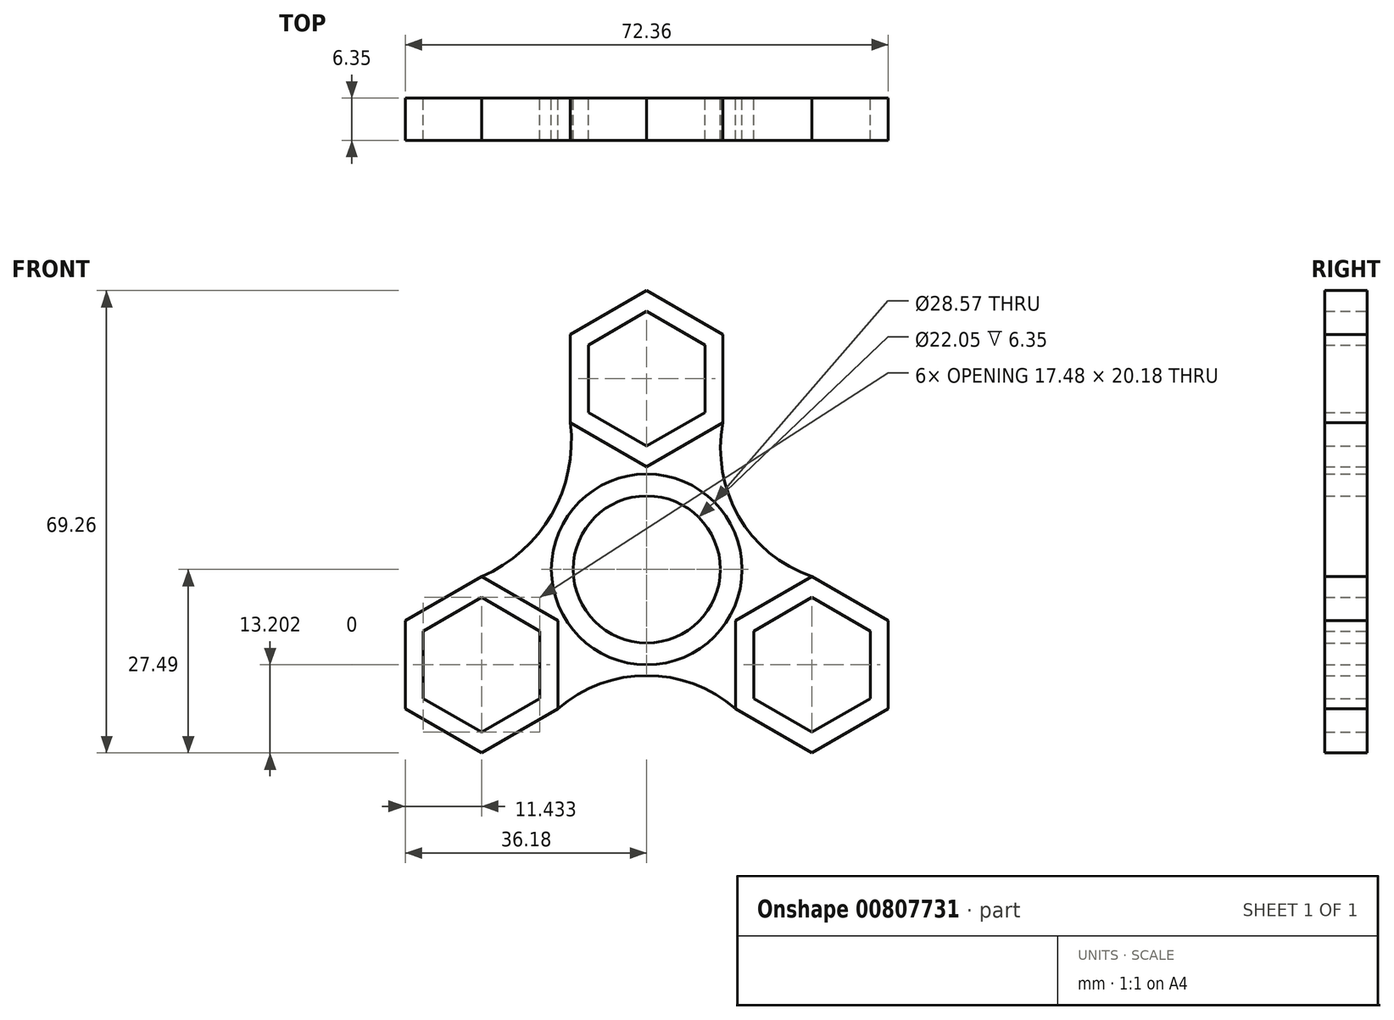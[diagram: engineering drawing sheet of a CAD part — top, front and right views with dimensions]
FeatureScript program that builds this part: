
annotation { "Feature Type Name" : "Feature", "Feature Type Description" : "" }
export const myFeature = defineFeature(function(context is Context, id is Id, definition is map)
    precondition{}
    {
        {
            var Q0;
            Q0=qCreatedBy(makeId("Front.planeOp"),FACE);
            var sketch = newSketch(context, id + "F0", { "sketchPlane" : qUnion([Q0])});
            skCircle(sketch, "E0", {"center": v(0, 0) * mm, "radius": 14.29 * mm});
            skCircle(sketch, "E1", {"center": v(0, 0) * mm, "radius": 11.02 * mm});
            skCircle(sketch, "E2.cCircle", {"center": v(0, 28.58) * mm, "radius": 8.74 * mm, "construction": true});
            skLineSegment(sketch, "E2.0", {"start": v(-8.74, 23.53) * mm, "end": v(-8.74, 33.62) * mm});
            skLineSegment(sketch, "E2.1", {"start": v(-8.74, 33.62) * mm, "end": v(0, 38.66) * mm});
            skLineSegment(sketch, "E2.2", {"start": v(0, 38.66) * mm, "end": v(8.74, 33.62) * mm});
            skLineSegment(sketch, "E2.3", {"start": v(8.74, 33.62) * mm, "end": v(8.74, 23.53) * mm});
            skLineSegment(sketch, "E2.4", {"start": v(8.74, 23.53) * mm, "end": v(0, 18.49) * mm});
            skLineSegment(sketch, "E2.5", {"start": v(0, 18.49) * mm, "end": v(-8.74, 23.53) * mm});
            skPoint(sketch, "E2.0.midPoint", {"position": v(-8.74, 28.58) * mm});
            skCircle(sketch, "E3.cCircle", {"center": v(0, 28.58) * mm, "radius": 11.43 * mm, "construction": true});
            skLineSegment(sketch, "E3.0", {"start": v(-11.43, 21.98) * mm, "end": v(-11.43, 35.17) * mm});
            skLineSegment(sketch, "E3.1", {"start": v(-11.43, 35.17) * mm, "end": v(0, 41.77) * mm});
            skLineSegment(sketch, "E3.2", {"start": v(0, 41.77) * mm, "end": v(11.43, 35.17) * mm});
            skLineSegment(sketch, "E3.3", {"start": v(11.43, 35.17) * mm, "end": v(11.43, 21.98) * mm});
            skLineSegment(sketch, "E3.4", {"start": v(11.43, 21.98) * mm, "end": v(0, 15.38) * mm});
            skLineSegment(sketch, "E3.5", {"start": v(0, 15.38) * mm, "end": v(-11.43, 21.98) * mm});
            skPoint(sketch, "E3.0.midPoint", {"position": v(-11.43, 28.58) * mm});
            skLineSegment(sketch, "E4.1.0", {"start": v(-24.75, -24.38) * mm, "end": v(-33.48, -19.33) * mm});
            skLineSegment(sketch, "E4.1.1", {"start": v(-36.18, -7.69) * mm, "end": v(-24.75, -1.09) * mm});
            skLineSegment(sketch, "E4.1.2", {"start": v(-24.75, -1.09) * mm, "end": v(-13.32, -7.69) * mm});
            skLineSegment(sketch, "E4.1.3", {"start": v(-13.32, -7.69) * mm, "end": v(-13.32, -20.89) * mm});
            skLineSegment(sketch, "E4.1.4", {"start": v(-33.48, -19.33) * mm, "end": v(-33.48, -9.24) * mm});
            skPoint(sketch, "E4.1.7", {"position": v(-19.03, -24.19) * mm});
            skCircle(sketch, "E4.1.8", {"center": v(-24.75, -14.29) * mm, "radius": 8.74 * mm, "construction": true});
            skLineSegment(sketch, "E4.1.9", {"start": v(-33.48, -9.24) * mm, "end": v(-24.75, -4.2) * mm});
            skLineSegment(sketch, "E4.1.10", {"start": v(-24.75, -4.2) * mm, "end": v(-16, -9.24) * mm});
            skLineSegment(sketch, "E4.1.11", {"start": v(-16, -9.24) * mm, "end": v(-16, -19.33) * mm});
            skCircle(sketch, "E4.1.12", {"center": v(-24.75, -14.29) * mm, "radius": 11.43 * mm, "construction": true});
            skLineSegment(sketch, "E4.1.13", {"start": v(-13.32, -20.89) * mm, "end": v(-24.75, -27.49) * mm});
            skLineSegment(sketch, "E4.1.14", {"start": v(-24.75, -27.49) * mm, "end": v(-36.18, -20.89) * mm});
            skLineSegment(sketch, "E4.1.15", {"start": v(-36.18, -20.89) * mm, "end": v(-36.18, -7.69) * mm});
            skPoint(sketch, "E4.1.16", {"position": v(-20.38, -21.85) * mm});
            skLineSegment(sketch, "E4.1.17", {"start": v(-16, -19.33) * mm, "end": v(-24.75, -24.38) * mm});
            skLineSegment(sketch, "E4.2.0", {"start": v(33.48, -9.24) * mm, "end": v(33.48, -19.33) * mm});
            skLineSegment(sketch, "E4.2.1", {"start": v(24.75, -27.49) * mm, "end": v(13.32, -20.89) * mm});
            skLineSegment(sketch, "E4.2.2", {"start": v(13.32, -20.89) * mm, "end": v(13.32, -7.69) * mm});
            skLineSegment(sketch, "E4.2.3", {"start": v(13.32, -7.69) * mm, "end": v(24.75, -1.09) * mm});
            skLineSegment(sketch, "E4.2.4", {"start": v(33.48, -19.33) * mm, "end": v(24.75, -24.38) * mm});
            skPoint(sketch, "E4.2.7", {"position": v(30.46, -4.39) * mm});
            skCircle(sketch, "E4.2.8", {"center": v(24.75, -14.29) * mm, "radius": 8.74 * mm, "construction": true});
            skLineSegment(sketch, "E4.2.9", {"start": v(24.75, -24.38) * mm, "end": v(16, -19.33) * mm});
            skLineSegment(sketch, "E4.2.10", {"start": v(16, -19.33) * mm, "end": v(16, -9.24) * mm});
            skLineSegment(sketch, "E4.2.11", {"start": v(16, -9.24) * mm, "end": v(24.75, -4.2) * mm});
            skCircle(sketch, "E4.2.12", {"center": v(24.75, -14.29) * mm, "radius": 11.43 * mm, "construction": true});
            skLineSegment(sketch, "E4.2.13", {"start": v(24.75, -1.09) * mm, "end": v(36.18, -7.69) * mm});
            skLineSegment(sketch, "E4.2.14", {"start": v(36.18, -7.69) * mm, "end": v(36.18, -20.89) * mm});
            skLineSegment(sketch, "E4.2.15", {"start": v(36.18, -20.89) * mm, "end": v(24.75, -27.49) * mm});
            skPoint(sketch, "E4.2.16", {"position": v(29.12, -6.72) * mm});
            skLineSegment(sketch, "E4.2.17", {"start": v(24.75, -4.2) * mm, "end": v(33.48, -9.24) * mm});
            skArc(sketch, "E5", {"start": v(11.43, 21.98) * mm, "mid": v(13.77, 7.95) * mm, "end": v(24.75, -1.09) * mm});
            skArc(sketch, "E6", {"start": v(-24.75, -1.09) * mm, "mid": v(-14.26, 8.23) * mm, "end": v(-11.43, 21.98) * mm});
            skArc(sketch, "E7", {"start": v(13.32, -20.89) * mm, "mid": v(0, -15.9) * mm, "end": v(-13.32, -20.89) * mm});
            skSolve(sketch);
        }
        {
            var Q0;
            Q0=makeQuery(id+"F0.imprint","IMPRINT",FACE,{"disambiguationData":[TD([[makeQuery(id+"F0.imprint","IMPRINT",EDGE,{"derivedFrom":sQuery(id+"F0.wireOp",EDGE,"E2.0")}),-1.0]])]});
            var sketch = newSketch(context, id + "F1", { "sketchPlane" : qUnion([Q0])});
            skArc(sketch, "E8", {"start": v(11.48, 22.04) * mm, "mid": v(12.38, 7.19) * mm, "end": v(24.77, -1.05) * mm});
            skArc(sketch, "E9", {"start": v(-24.76, -1.04) * mm, "mid": v(-12.38, 7.18) * mm, "end": v(-11.44, 22) * mm});
            skArc(sketch, "E10", {"start": v(13.38, -20.88) * mm, "mid": v(0.07, -14.3) * mm, "end": v(-13.26, -20.84) * mm});
            skSolve(sketch);
        }
        {
            var Q0;
            Q0 = qSketchRegion(id + "F1", true);
            var Q1;
            Q1=makeQuery(id+"F0.imprint","IMPRINT",FACE,{"disambiguationData":[TD([[makeQuery(id+"F0.imprint","IMPRINT",EDGE,{"derivedFrom":sQuery(id+"F0.wireOp",EDGE,"E4.1.0")}),1.0]])]});
            var Q2;
            Q2=makeQuery(id+"F0.imprint","IMPRINT",FACE,{"disambiguationData":[TD([[makeQuery(id+"F0.imprint","IMPRINT",EDGE,{"derivedFrom":sQuery(id+"F0.wireOp",EDGE,"E4.2.0")}),1.0]])]});
            var Q3;
            Q3=makeQuery(id+"F0.imprint","IMPRINT",FACE,{"disambiguationData":[TD([[makeQuery(id+"F0.imprint","IMPRINT",EDGE,{"derivedFrom":sQuery(id+"F0.wireOp",EDGE,"E2.0")}),1.0]])]});
            var Q4;
            Q4=makeQuery(id+"F0.imprint","IMPRINT",FACE,{"disambiguationData":[TD([[makeQuery(id+"F0.imprint","IMPRINT",EDGE,{"derivedFrom":sQuery(id+"F0.wireOp",EDGE,"E0")}),1.0]])]});
            extrude(context, id + "F2", {"entities" : qUnion([Q0, Q1, Q2, Q3, Q4]), "depth" : 6.35 * mm, "offsetDistance" : 25.4 * mm});
        }
        {
            var Q0;
            Q0 = qSketchRegion(id + "F0", true);
            extrude(context, id + "F3", {"entities" : qUnion([Q0]), "depth" : 6.35 * mm, "offsetDistance" : 25.4 * mm});
        }
    });
